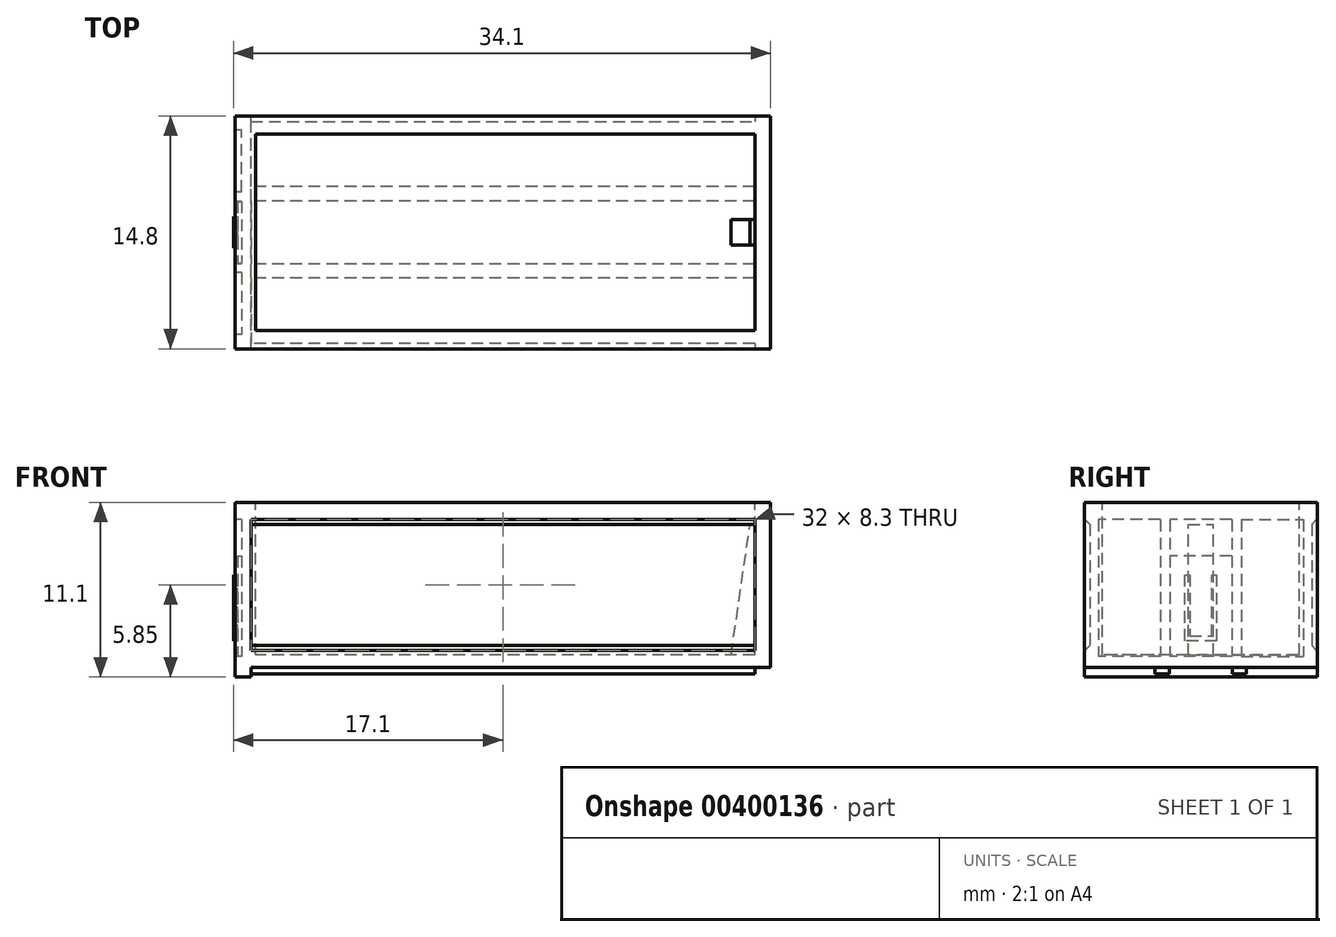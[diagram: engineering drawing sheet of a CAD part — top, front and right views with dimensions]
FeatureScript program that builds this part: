
annotation { "Feature Type Name" : "Feature", "Feature Type Description" : "" }
export const myFeature = defineFeature(function(context is Context, id is Id, definition is map)
    precondition{}
    {
        {
            var Q0;
            Q0=qCreatedBy(makeId("Right.planeOp"),FACE);
            var sketch = newSketch(context, id + "F0", { "sketchPlane" : qUnion([Q0])});
            skLineSegment(sketch, "E0", {"start": v(-7.4, 10.9) * mm, "end": v(-7.4, 9.8) * mm});
            skLineSegment(sketch, "E1", {"start": v(-7.4, 9.8) * mm, "end": v(-7.05, 9.8) * mm});
            skLineSegment(sketch, "E2", {"start": v(-7.05, 9.8) * mm, "end": v(-7.05, 1.5) * mm});
            skLineSegment(sketch, "E3", {"start": v(-7.05, 1.5) * mm, "end": v(-7.4, 1.5) * mm});
            skLineSegment(sketch, "E4", {"start": v(-7.4, 1.5) * mm, "end": v(-7.4, 0.4) * mm});
            skLineSegment(sketch, "E5", {"start": v(-2.9, 0) * mm, "end": v(-2, 0) * mm});
            skLineSegment(sketch, "E6", {"start": v(0, 0.4) * mm, "end": v(0, 1.2) * mm});
            skLineSegment(sketch, "E7", {"start": v(0, 1.2) * mm, "end": v(-6.25, 1.2) * mm});
            skLineSegment(sketch, "E8", {"start": v(-6.25, 1.2) * mm, "end": v(-6.25, 10.9) * mm});
            skLineSegment(sketch, "E9", {"start": v(-6.25, 10.9) * mm, "end": v(-7.4, 10.9) * mm});
            skLineSegment(sketch, "E10", {"start": v(0, 0.4) * mm, "end": v(-2, 0.4) * mm});
            skLineSegment(sketch, "E11", {"start": v(-2, 0.4) * mm, "end": v(-2, 0) * mm});
            skLineSegment(sketch, "E12", {"start": v(-2.9, 0) * mm, "end": v(-2.9, 0.4) * mm});
            skLineSegment(sketch, "E13", {"start": v(-2.9, 0.4) * mm, "end": v(-7.4, 0.4) * mm});
            skLineSegment(sketch, "E14", {"start": v(0, 0) * mm, "end": v(0, -3.4) * mm, "construction": true});
            skSolve(sketch);
        }
        {
            var Q0;
            Q0 = qSketchRegion(id + "F0", true);
            extrude(context, id + "F1", {"entities" : qUnion([Q0]), "depth" : 32 * mm, "offsetDistance" : 25 * mm});
        }
        {
            var Q0;
            Q0=makeQuery(id+"F1.opExtrude","SWEPT_FACE",FACE,{"disambiguationData":[OSD([sQuery(id+"F0.wireOp",EDGE,"E0")])]});
            var sketch = newSketch(context, id + "F2", { "sketchPlane" : qUnion([Q0])});
            skLineSegment(sketch, "E15.bottom", {"start": v(32, 10.9) * mm, "end": v(33, 10.9) * mm});
            skLineSegment(sketch, "E15.top", {"start": v(32, 0.4) * mm, "end": v(33, 0.4) * mm});
            skLineSegment(sketch, "E15.left", {"start": v(32, 10.9) * mm, "end": v(32, 0.4) * mm});
            skLineSegment(sketch, "E15.right", {"start": v(33, 10.9) * mm, "end": v(33, 0.4) * mm});
            skSolve(sketch);
        }
        {
            var Q0;
            Q0 = qSketchRegion(id + "F2", true);
            var Q1;
            Q1=makeQuery(id+"F1.opExtrude","SWEPT_FACE",FACE,{"disambiguationData":[OSD([sQuery(id+"F0.wireOp",EDGE,"E6")])]});
            extrude(context, id + "F3", {"entities" : qUnion([Q0]), "operationType" : NewBodyOperationType.ADD, "endBound" : BoundingType.UP_TO_SURFACE, "oppositeDirection" : true, "depth" : 25 * mm, "endBoundEntityFace" : qUnion([Q1]), "offsetDistance" : 25 * mm});
        }
        {
            var Q0;
            Q0=makeQuery(id+"F1.opExtrude","CAP_FACE",FACE,{"disambiguationData":[OSD([sQuery(id+"F0.wireOp",EDGE,"E0"),sQuery(id+"F0.wireOp",EDGE,"E1"),sQuery(id+"F0.wireOp",EDGE,"E2"),sQuery(id+"F0.wireOp",EDGE,"E3"),sQuery(id+"F0.wireOp",EDGE,"E4"),sQuery(id+"F0.wireOp",EDGE,"E5"),sQuery(id+"F0.wireOp",EDGE,"E6"),sQuery(id+"F0.wireOp",EDGE,"E7"),sQuery(id+"F0.wireOp",EDGE,"E8"),sQuery(id+"F0.wireOp",EDGE,"E9"),sQuery(id+"F0.wireOp",EDGE,"E10"),sQuery(id+"F0.wireOp",EDGE,"E11"),sQuery(id+"F0.wireOp",EDGE,"E12"),sQuery(id+"F0.wireOp",EDGE,"E13")])],"isStart":true});
            var sketch = newSketch(context, id + "F4", { "sketchPlane" : qUnion([Q0])});
            skLineSegment(sketch, "E16.bottom", {"start": v(7.4, 10.9) * mm, "end": v(0, 10.9) * mm});
            skLineSegment(sketch, "E16.top", {"start": v(7.4, 0) * mm, "end": v(0, 0) * mm});
            skLineSegment(sketch, "E16.left", {"start": v(7.4, 10.9) * mm, "end": v(7.4, 0) * mm});
            skLineSegment(sketch, "E16.right", {"start": v(0, 10.9) * mm, "end": v(0, 0) * mm});
            skSolve(sketch);
        }
        {
            var Q0;
            Q0 = qSketchRegion(id + "F4", true);
            extrude(context, id + "F5", {"entities" : qUnion([Q0]), "operationType" : NewBodyOperationType.ADD, "depth" : 1 * mm, "offsetDistance" : 25 * mm});
        }
        {
            var Q0;
            Q0=makeQuery(id+"F5.opExtrude","CAP_FACE",FACE,{"disambiguationData":[OSD([sQuery(id+"F4.wireOp",EDGE,"E16.bottom"),sQuery(id+"F4.wireOp",EDGE,"E16.top"),sQuery(id+"F4.wireOp",EDGE,"E16.left"),sQuery(id+"F4.wireOp",EDGE,"E16.right")])],"isStart":false});
            var sketch = newSketch(context, id + "F6", { "sketchPlane" : qUnion([Q0])});
            skLineSegment(sketch, "E17.bottom", {"start": v(2.57, 9.8) * mm, "end": v(6.5, 9.8) * mm});
            skLineSegment(sketch, "E17.top", {"start": v(2.57, 1.1) * mm, "end": v(6.5, 1.1) * mm});
            skLineSegment(sketch, "E17.left", {"start": v(2.57, 9.8) * mm, "end": v(2.57, 1.1) * mm});
            skLineSegment(sketch, "E17.right", {"start": v(6.5, 9.8) * mm, "end": v(6.5, 1.1) * mm});
            skLineSegment(sketch, "E18.bottom", {"start": v(0, 9.8) * mm, "end": v(1.97, 9.8) * mm});
            skLineSegment(sketch, "E18.top", {"start": v(0, 1.1) * mm, "end": v(1.97, 1.1) * mm});
            skLineSegment(sketch, "E18.left", {"start": v(0, 9.8) * mm, "end": v(0, 1.1) * mm});
            skLineSegment(sketch, "E18.right", {"start": v(1.97, 9.8) * mm, "end": v(1.97, 1.1) * mm});
            skLineSegment(sketch, "E19", {"start": v(4.53, 9.8) * mm, "end": v(4.53, 5.01) * mm, "construction": true});
            skLineSegment(sketch, "E20", {"start": v(4.53, 5.01) * mm, "end": v(2.57, 5.01) * mm, "construction": true});
            skLineSegment(sketch, "E21", {"start": v(1.97, 5.01) * mm, "end": v(0, 5.01) * mm, "construction": true});
            skSolve(sketch);
        }
        {
            var Q0;
            Q0 = qSketchRegion(id + "F6", true);
            extrude(context, id + "F7", {"entities" : qUnion([Q0]), "operationType" : NewBodyOperationType.REMOVE, "oppositeDirection" : true, "depth" : 0.4 * mm, "offsetDistance" : 25 * mm});
        }
        {
            var Q0;
            Q0=makeQuery(id+"F1.opExtrude","SWEPT_EDGE",EDGE,{"disambiguationData":[OSD([sQuery(id+"F0.wireOp",EDGE,"E2"),sQuery(id+"F0.wireOp",EDGE,"E3")])]});
            var Q1;
            Q1=makeQuery(id+"F1.opExtrude","SWEPT_EDGE",EDGE,{"disambiguationData":[OSD([sQuery(id+"F0.wireOp",EDGE,"E1"),sQuery(id+"F0.wireOp",EDGE,"E2")])]});
            chamfer(context, id + "F8", {"entities" : qUnion([Q0, Q1]), "width" : 0.3 * mm, "tangentPropagation" : true});
        }
        {
            var Q0;
            {var subQ0=sQuery(id+"F0.wireOp",EDGE,"E6");Q0=makeQuery(id+"F5.boolean.opBoolean","MERGE",FACE,{"derivedFrom":[makeQuery(id+"F3.boolean.opBoolean","MERGE",FACE,{"derivedFrom":[makeQuery(id+"F1.opExtrude","SWEPT_FACE",FACE,{"disambiguationData":[OSD([subQ0])]}),makeQuery(id+"F3.opExtrude","CAP_FACE",FACE,{"disambiguationData":[OSD([subQ0])],"isStart":false})]}),makeQuery(id+"F5.opExtrude","SWEPT_FACE",FACE,{"disambiguationData":[OSD([sQuery(id+"F4.wireOp",EDGE,"E16.right")])]})]});}
            var sketch = newSketch(context, id + "F9", { "sketchPlane" : qUnion([Q0])});
            skLineSegment(sketch, "E22", {"start": v(-32, 1.2) * mm, "end": v(-30.5, 1.2) * mm});
            skLineSegment(sketch, "E23", {"start": v(-30.5, 1.2) * mm, "end": v(-31.7, 9.5) * mm});
            skLineSegment(sketch, "E24", {"start": v(-31.7, 9.5) * mm, "end": v(-32, 9.5) * mm});
            skLineSegment(sketch, "E25", {"start": v(-32, 9.5) * mm, "end": v(-32, 1.2) * mm});
            skSolve(sketch);
        }
        {
            var Q0;
            Q0 = qSketchRegion(id + "F9", true);
            extrude(context, id + "F10", {"entities" : qUnion([Q0]), "operationType" : NewBodyOperationType.ADD, "oppositeDirection" : true, "depth" : 0.8 * mm, "offsetDistance" : 25 * mm});
        }
        {
            var Q0;
            Q0=makeQuery(id+"F1.opExtrude","SWEPT_BODY",BODY,{"disambiguationData":[OSD([sQuery(id+"F0.wireOp",EDGE,"E0"),sQuery(id+"F0.wireOp",EDGE,"E1"),sQuery(id+"F0.wireOp",EDGE,"E2"),sQuery(id+"F0.wireOp",EDGE,"E3"),sQuery(id+"F0.wireOp",EDGE,"E4"),sQuery(id+"F0.wireOp",EDGE,"E5"),sQuery(id+"F0.wireOp",EDGE,"E6"),sQuery(id+"F0.wireOp",EDGE,"E7"),sQuery(id+"F0.wireOp",EDGE,"E8"),sQuery(id+"F0.wireOp",EDGE,"E9"),sQuery(id+"F0.wireOp",EDGE,"E10"),sQuery(id+"F0.wireOp",EDGE,"E11"),sQuery(id+"F0.wireOp",EDGE,"E12"),sQuery(id+"F0.wireOp",EDGE,"E13")])]});
            var Q1;
            {var subQ0=sQuery(id+"F0.wireOp",EDGE,"E6");Q1=makeQuery(id+"F10.boolean.opBoolean","MERGE",FACE,{"derivedFrom":[makeQuery(id+"F5.boolean.opBoolean","MERGE",FACE,{"derivedFrom":[makeQuery(id+"F3.boolean.opBoolean","MERGE",FACE,{"derivedFrom":[makeQuery(id+"F1.opExtrude","SWEPT_FACE",FACE,{"disambiguationData":[OSD([subQ0])]}),makeQuery(id+"F3.opExtrude","CAP_FACE",FACE,{"disambiguationData":[OSD([subQ0])],"isStart":false})]}),makeQuery(id+"F5.opExtrude","SWEPT_FACE",FACE,{"disambiguationData":[OSD([sQuery(id+"F4.wireOp",EDGE,"E16.right")])]})]}),makeQuery(id+"F10.opExtrude","CAP_FACE",FACE,{"disambiguationData":[OSD([sQuery(id+"F9.wireOp",EDGE,"8C4jzjjI-H8TU-Mi3Z-EukI-BTS6VJ2B2IYy"),sQuery(id+"F9.wireOp",EDGE,"OC46rUm6-lAtg-VFpL-xiZC-udKdomprociL"),sQuery(id+"F9.wireOp",EDGE,"OR3EWEKU-YdXa-Ozdm-wm0I-Usp0X4Bevzxc"),sQuery(id+"F9.wireOp",EDGE,"YwbCKrvN-EAOm-X432-ycXu-IHhjAEk5w7Bi")])],"isStart":true})]});}
            mirror(context, id + "F11", {"operationType" : NewBodyOperationType.ADD, "entities" : qUnion([Q0]), "mirrorPlane" : qUnion([Q1])});
        }
        {
            var Q0;
            {var subQ0=makeQuery(id+"F5.boolean.opBoolean","MERGE",FACE,{"derivedFrom":[makeQuery(id+"F1.opExtrude","SWEPT_FACE",FACE,{"disambiguationData":[OSD([sQuery(id+"F0.wireOp",EDGE,"E5")])]}),makeQuery(id+"F5.opExtrude","SWEPT_FACE",FACE,{"disambiguationData":[OSD([sQuery(id+"F4.wireOp",EDGE,"E16.top")])]})]});Q0=makeQuery(id+"F11.boolean.opBoolean","MERGE",FACE,{"derivedFrom":[subQ0,makeQuery(id+"F11.opPattern","COPY",FACE,{"derivedFrom":subQ0,"instanceName":"1"})]});}
            var sketch = newSketch(context, id + "F12", { "sketchPlane" : qUnion([Q0])});
            skLineSegment(sketch, "E26.bottom", {"start": v(0, -7.4) * mm, "end": v(-1, -7.4) * mm});
            skLineSegment(sketch, "E26.top", {"start": v(0, 7.4) * mm, "end": v(-1, 7.4) * mm});
            skLineSegment(sketch, "E26.left", {"start": v(0, -7.4) * mm, "end": v(0, 7.4) * mm});
            skLineSegment(sketch, "E26.right", {"start": v(-1, -7.4) * mm, "end": v(-1, 7.4) * mm});
            skSolve(sketch);
        }
        {
            var Q0;
            Q0 = qSketchRegion(id + "F12", true);
            extrude(context, id + "F13", {"entities" : qUnion([Q0]), "operationType" : NewBodyOperationType.ADD, "depth" : 0.2 * mm, "offsetDistance" : 25 * mm});
        }
        {
            var Q0;
            {var subQ0=sQuery(id+"F4.wireOp",EDGE,"E16.right");var subQ2=sQuery(id+"F4.wireOp",EDGE,"E16.bottom");var subQ3=makeQuery(id+"F5.boolean.opBoolean","SPLIT",FACE,{"disambiguationData":[TD([makeQuery(id+"F1.opExtrude","SWEPT_FACE",FACE,{"disambiguationData":[OSD([sQuery(id+"F0.wireOp",EDGE,"E7")])]})])],"derivedFrom":makeQuery(id+"F5.opExtrude","CAP_FACE",FACE,{"disambiguationData":[OSD([subQ2,sQuery(id+"F4.wireOp",EDGE,"E16.top"),sQuery(id+"F4.wireOp",EDGE,"E16.left"),subQ0])],"isStart":true})});Q0=makeQuery(id+"F11.boolean.opBoolean","MERGE",FACE,{"derivedFrom":[subQ3,makeQuery(id+"F11.opPattern","COPY",FACE,{"derivedFrom":subQ3,"instanceName":"1"})]});}
            extrude(context, id + "F14", {"entities" : qUnion([Q0]), "operationType" : NewBodyOperationType.ADD, "depth" : 0.3 * mm, "offsetDistance" : 25 * mm});
        }
        {
            var Q0;
            {var subQ0=makeQuery(id+"F7.boolean.opBoolean","COPY",FACE,{"derivedFrom":makeQuery(id+"F7.opExtrude","CAP_FACE",FACE,{"disambiguationData":[OSD([sQuery(id+"F6.wireOp",EDGE,"E18.bottom"),sQuery(id+"F6.wireOp",EDGE,"E18.top"),sQuery(id+"F6.wireOp",EDGE,"E18.left"),sQuery(id+"F6.wireOp",EDGE,"E18.right")])],"isStart":false})});Q0=makeQuery(id+"F11.boolean.opBoolean","MERGE",FACE,{"derivedFrom":[subQ0,makeQuery(id+"F11.opPattern","COPY",FACE,{"derivedFrom":subQ0,"instanceName":"1"})]});}
            var sketch = newSketch(context, id + "F15", { "sketchPlane" : qUnion([Q0])});
            skLineSegment(sketch, "E27.bottom", {"start": v(-1.97, 1.1) * mm, "end": v(1.97, 1.1) * mm});
            skLineSegment(sketch, "E27.top", {"start": v(-1.97, 7.5) * mm, "end": v(1.97, 7.5) * mm});
            skLineSegment(sketch, "E27.left", {"start": v(-1.97, 1.1) * mm, "end": v(-1.97, 7.5) * mm});
            skLineSegment(sketch, "E27.right", {"start": v(1.97, 1.1) * mm, "end": v(1.97, 7.5) * mm});
            skSolve(sketch);
        }
        {
            var Q0;
            Q0 = qSketchRegion(id + "F15", true);
            extrude(context, id + "F16", {"entities" : qUnion([Q0]), "operationType" : NewBodyOperationType.ADD, "depth" : 0.25 * mm, "offsetDistance" : 25 * mm});
        }
        {
            var Q0;
            Q0=makeQuery(id+"F16.opExtrude","CAP_FACE",FACE,{"disambiguationData":[OSD([sQuery(id+"F15.wireOp",EDGE,"E27.bottom"),sQuery(id+"F15.wireOp",EDGE,"E27.top"),sQuery(id+"F15.wireOp",EDGE,"E27.left"),sQuery(id+"F15.wireOp",EDGE,"E27.right")])],"isStart":false});
            var sketch = newSketch(context, id + "F17", { "sketchPlane" : qUnion([Q0])});
            skLineSegment(sketch, "E28", {"start": v(-1, 6.3) * mm, "end": v(-1, 2.1) * mm});
            skLineSegment(sketch, "E29", {"start": v(-1, 2.1) * mm, "end": v(1, 2.1) * mm});
            skLineSegment(sketch, "E30", {"start": v(1, 2.1) * mm, "end": v(1, 6.3) * mm});
            skLineSegment(sketch, "E31", {"start": v(1, 6.3) * mm, "end": v(0.7, 6.3) * mm});
            skLineSegment(sketch, "E32", {"start": v(0.7, 6.3) * mm, "end": v(0.7, 2.4) * mm});
            skLineSegment(sketch, "E33", {"start": v(0.7, 2.4) * mm, "end": v(-0.7, 2.4) * mm});
            skLineSegment(sketch, "E34", {"start": v(-0.7, 2.4) * mm, "end": v(-0.7, 6.3) * mm});
            skLineSegment(sketch, "E35", {"start": v(-0.7, 6.3) * mm, "end": v(-1, 6.3) * mm});
            skLineSegment(sketch, "E36", {"start": v(0, 2.1) * mm, "end": v(0, 1.1) * mm, "construction": true});
            skSolve(sketch);
        }
        {
            var Q0;
            Q0 = qSketchRegion(id + "F17", true);
            extrude(context, id + "F18", {"entities" : qUnion([Q0]), "operationType" : NewBodyOperationType.ADD, "depth" : 0.25 * mm, "offsetDistance" : 25 * mm});
        }
    });
